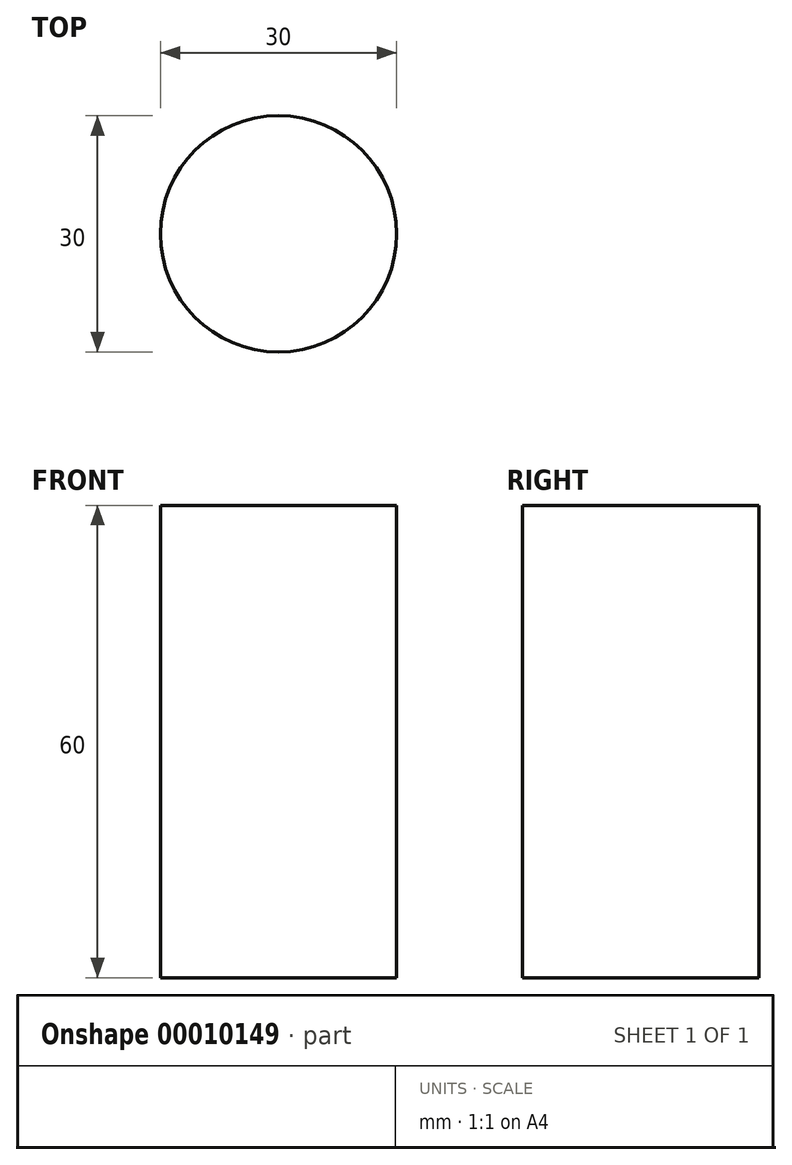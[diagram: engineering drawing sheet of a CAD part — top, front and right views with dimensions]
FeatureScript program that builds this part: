
annotation { "Feature Type Name" : "Feature", "Feature Type Description" : "" }
export const myFeature = defineFeature(function(context is Context, id is Id, definition is map)
    precondition{}
    {
        {
            var Q0;
            Q0=qCreatedBy(makeId("Top.planeOp"),FACE);
            var sketch = newSketch(context, id + "F0", { "sketchPlane" : qUnion([Q0])});
            skCircle(sketch, "E0", {"center": v(0, 0) * mm, "radius": 15 * mm});
            skSolve(sketch);
        }
        {
            var Q0;
            Q0=makeQuery(id+"F0.imprint","IMPRINT",FACE,{"disambiguationData":[TD([[makeQuery(id+"F0.imprint","IMPRINT",EDGE,{"derivedFrom":sQuery(id+"F0.wireOp",EDGE,"E0")}),1.0]])]});
            extrude(context, id + "F1", {"entities" : qUnion([Q0]), "depth" : 60 * mm});
        }
    });
